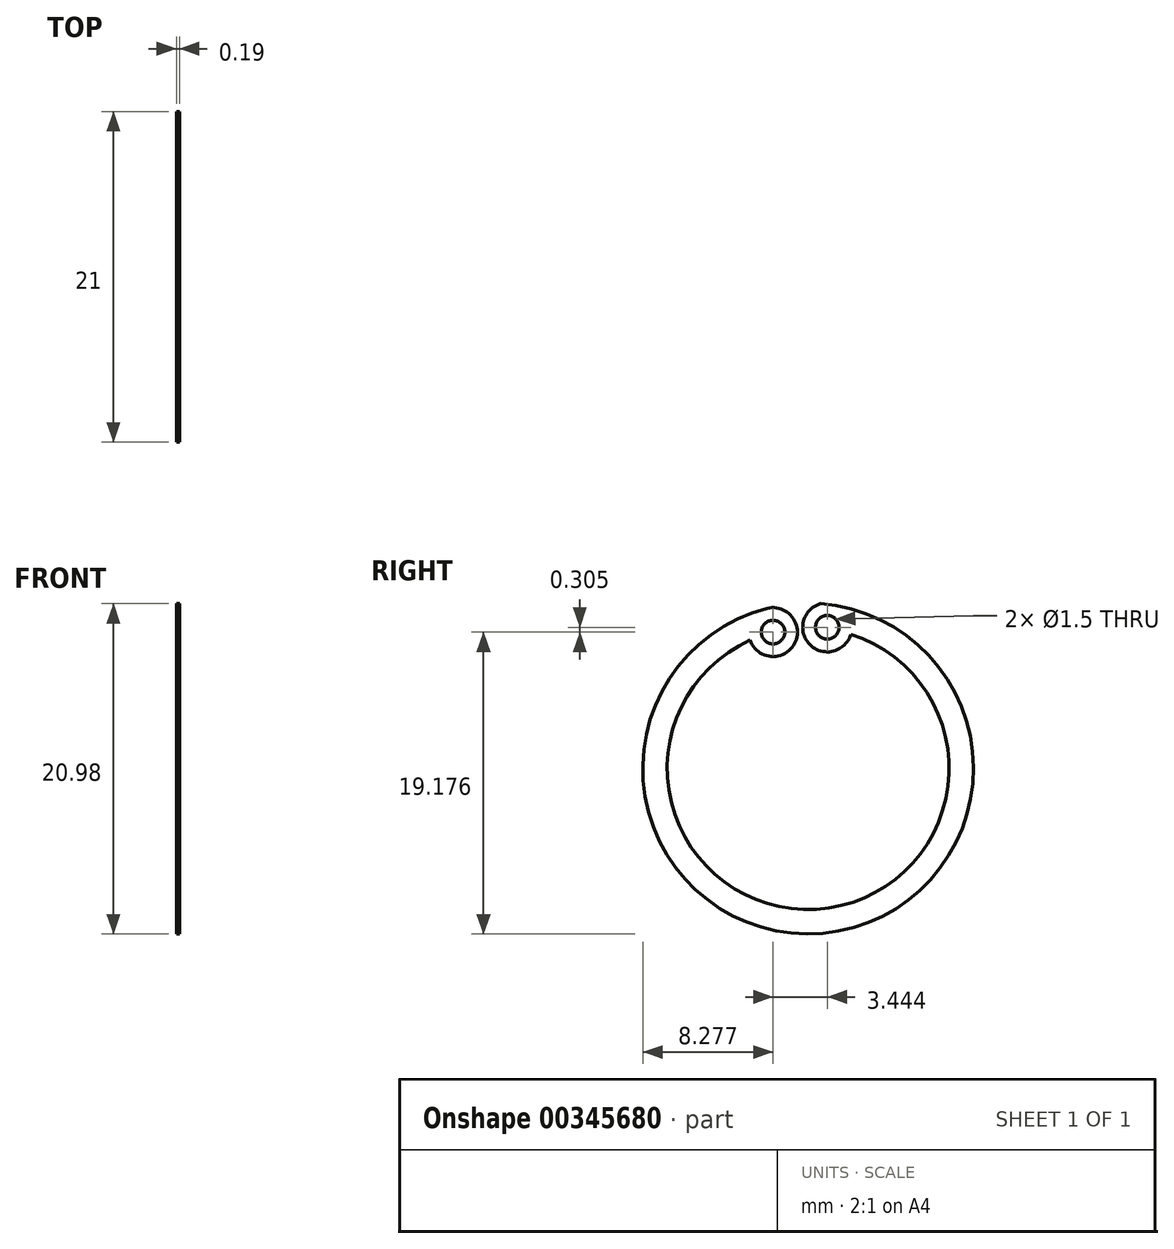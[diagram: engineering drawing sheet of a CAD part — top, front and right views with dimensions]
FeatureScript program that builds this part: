
annotation { "Feature Type Name" : "Feature", "Feature Type Description" : "" }
export const myFeature = defineFeature(function(context is Context, id is Id, definition is map)
    precondition{}
    {
        {
            var Q0;
            Q0=qCreatedBy(makeId("Right.planeOp"),FACE);
            var sketch = newSketch(context, id + "F0", { "sketchPlane" : qUnion([Q0])});
            skArc(sketch, "E0", {"start": v(-30.25, 51.15) * mm, "mid": v(-26.7, 30.52) * mm, "end": v(-26.86, 51.45) * mm});
            skLineSegment(sketch, "E1", {"start": v(-30.25, 51.15) * mm, "end": v(-30.25, 51.14) * mm});
            skArc(sketch, "E2", {"start": v(-31.32, 49.13) * mm, "mid": v(-28.5, 48.92) * mm, "end": v(-30.25, 51.15) * mm});
            skPoint(sketch, "E3.orphan", {"position": v(-26.86, 51.45) * mm});
            skArc(sketch, "E4", {"start": v(-26.86, 51.45) * mm, "mid": v(-27.52, 48.85) * mm, "end": v(-24.92, 49.5) * mm});
            skArc(sketch, "E5.trimOffspring", {"start": v(-31.32, 49.13) * mm, "mid": v(-27.12, 32.04) * mm, "end": v(-24.92, 49.5) * mm});
            skCircle(sketch, "E6", {"center": v(-29.86, 49.65) * mm, "radius": 0.75 * mm});
            skCircle(sketch, "E7", {"center": v(-26.42, 49.95) * mm, "radius": 0.75 * mm});
            skPoint(sketch, "E8.center.orphan", {"position": v(-30.06, 50.4) * mm});
            skPoint(sketch, "E9.center.orphan", {"position": v(-26.86, 50.67) * mm});
            skPoint(sketch, "E10.trimOffspring.end.orphan", {"position": v(-26.86, 49.9) * mm});
            skSolve(sketch);
        }
        {
            var Q0;
            Q0=qSketchRegion(id+"F0",true);
            extrude(context, id + "F1", {"entities" : qUnion([Q0]), "depth" : .19 * mm});
        }
    });
